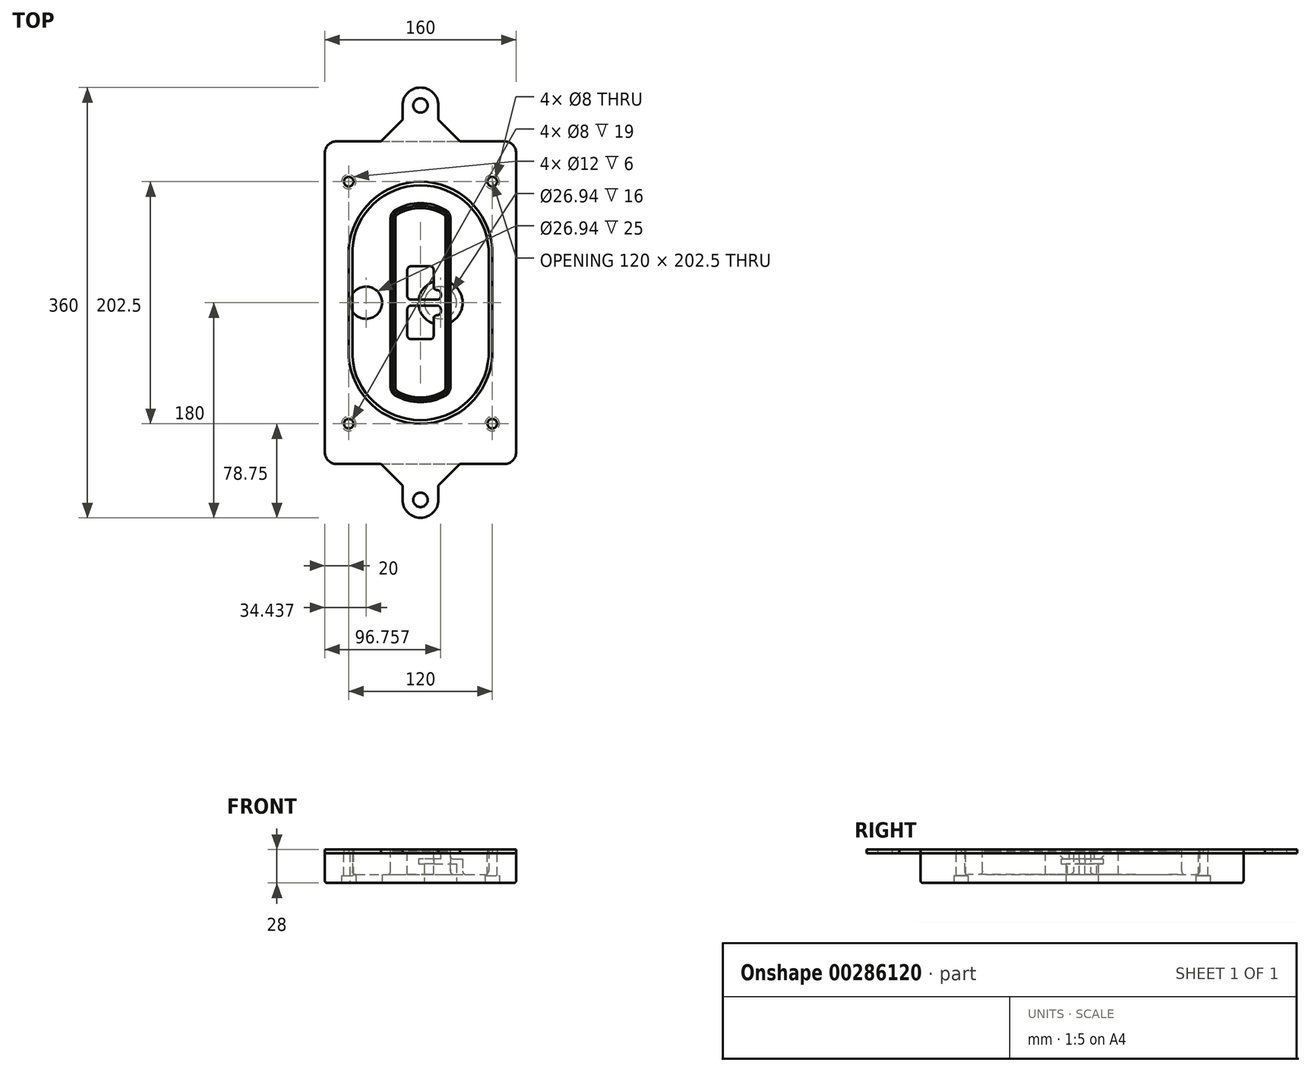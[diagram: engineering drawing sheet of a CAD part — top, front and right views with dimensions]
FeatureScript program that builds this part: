
annotation { "Feature Type Name" : "Feature", "Feature Type Description" : "" }
export const myFeature = defineFeature(function(context is Context, id is Id, definition is map)
    precondition{}
    {
        {
            var Q0;
            Q0=qCreatedBy(makeId("Top.planeOp"),FACE);
            var sketch = newSketch(context, id + "F0", { "sketchPlane" : qUnion([Q0])});
            skPoint(sketch, "E0.rect.middle", {"position": v(0, 0) * mm});
            skLineSegment(sketch, "E1.bottom", {"start": v(-70, -135) * mm, "end": v(70, -135) * mm});
            skLineSegment(sketch, "E1.top", {"start": v(-70, 135) * mm, "end": v(70, 135) * mm});
            skLineSegment(sketch, "E1.left", {"start": v(-80, -125) * mm, "end": v(-80, 125) * mm});
            skLineSegment(sketch, "E1.right", {"start": v(80, -125) * mm, "end": v(80, 125) * mm});
            skLineSegment(sketch, "E2", {"start": v(-80, 135) * mm, "end": v(80, -135) * mm, "construction": true});
            skLineSegment(sketch, "E3", {"start": v(80, 135) * mm, "end": v(-80, -135) * mm, "construction": true});
            skCircle(sketch, "E4", {"center": v(-60, 101.25) * mm, "radius": 4 * mm});
            skCircle(sketch, "E5", {"center": v(60, 101.25) * mm, "radius": 4 * mm});
            skCircle(sketch, "E6", {"center": v(60, -101.25) * mm, "radius": 4 * mm});
            skCircle(sketch, "E7", {"center": v(-60, -101.25) * mm, "radius": 4 * mm});
            skLineSegment(sketch, "E8", {"start": v(-60, 101.25) * mm, "end": v(60, 101.25) * mm, "construction": true});
            skLineSegment(sketch, "E9", {"start": v(60, 101.25) * mm, "end": v(60, -101.25) * mm, "construction": true});
            skLineSegment(sketch, "E10", {"start": v(60, -101.25) * mm, "end": v(-60, -101.25) * mm, "construction": true});
            skLineSegment(sketch, "E11", {"start": v(-60, -101.25) * mm, "end": v(-60, 101.25) * mm, "construction": true});
            skLineSegment(sketch, "E12", {"start": v(-60, 44.66) * mm, "end": v(-60, -44.66) * mm});
            skLineSegment(sketch, "E13", {"start": v(60, 44.66) * mm, "end": v(60, -44.66) * mm});
            skArc(sketch, "E14", {"start": v(59.98, 45.37) * mm, "mid": v(0, 101.25) * mm, "end": v(-59.98, 45.37) * mm});
            skArc(sketch, "E15", {"start": v(-59.98, -45.37) * mm, "mid": v(0, -101.25) * mm, "end": v(59.98, -45.37) * mm});
            skLineSegment(sketch, "E16", {"start": v(-60, 0) * mm, "end": v(60, 0) * mm, "construction": true});
            skPoint(sketch, "E17.visualSharp", {"position": v(-60, -45) * mm});
            skArc(sketch, "E17.filletArc", {"start": v(-60, -44.66) * mm, "mid": v(-60, -45.02) * mm, "end": v(-59.98, -45.37) * mm});
            skPoint(sketch, "E18.visualSharp", {"position": v(-60, 45) * mm});
            skArc(sketch, "E18.filletArc", {"start": v(-59.98, 45.37) * mm, "mid": v(-60, 45.02) * mm, "end": v(-60, 44.66) * mm});
            skPoint(sketch, "E19.visualSharp", {"position": v(60, 45) * mm});
            skArc(sketch, "E19.filletArc", {"start": v(60, 44.66) * mm, "mid": v(60, 45.02) * mm, "end": v(59.98, 45.37) * mm});
            skPoint(sketch, "E20.visualSharp", {"position": v(60, -45) * mm});
            skArc(sketch, "E20.filletArc", {"start": v(59.98, -45.37) * mm, "mid": v(60, -45.02) * mm, "end": v(60, -44.66) * mm});
            skPoint(sketch, "E21.visualSharp", {"position": v(-80, 135) * mm});
            skArc(sketch, "E21.filletArc", {"start": v(-70, 135) * mm, "mid": v(-77.07, 132.07) * mm, "end": v(-80, 125) * mm});
            skPoint(sketch, "E22.visualSharp", {"position": v(80, 135) * mm});
            skArc(sketch, "E22.filletArc", {"start": v(80, 125) * mm, "mid": v(77.07, 132.07) * mm, "end": v(70, 135) * mm});
            skPoint(sketch, "E23.visualSharp", {"position": v(80, -135) * mm});
            skArc(sketch, "E23.filletArc", {"start": v(70, -135) * mm, "mid": v(77.07, -132.07) * mm, "end": v(80, -125) * mm});
            skPoint(sketch, "E24.visualSharp", {"position": v(-80, -135) * mm});
            skArc(sketch, "E24.filletArc", {"start": v(-80, -125) * mm, "mid": v(-77.07, -132.07) * mm, "end": v(-70, -135) * mm});
            skArc(sketch, "E25.0", {"start": v(57, 44.66) * mm, "mid": v(57, 44.9) * mm, "end": v(56.98, 45.16) * mm});
            skLineSegment(sketch, "E25.1", {"start": v(57, 44.66) * mm, "end": v(57, -44.66) * mm});
            skArc(sketch, "E25.2", {"start": v(56.98, -45.16) * mm, "mid": v(57, -44.9) * mm, "end": v(57, -44.66) * mm});
            skArc(sketch, "E25.3", {"start": v(-56.98, -45.16) * mm, "mid": v(0, -98.25) * mm, "end": v(56.98, -45.16) * mm});
            skArc(sketch, "E25.4", {"start": v(-57, -44.66) * mm, "mid": v(-57, -44.9) * mm, "end": v(-56.98, -45.16) * mm});
            skArc(sketch, "E25.5", {"start": v(56.98, 45.16) * mm, "mid": v(0, 98.25) * mm, "end": v(-56.98, 45.16) * mm});
            skLineSegment(sketch, "E25.6", {"start": v(-57, 44.66) * mm, "end": v(-57, -44.66) * mm});
            skArc(sketch, "E25.7", {"start": v(-56.98, 45.16) * mm, "mid": v(-57, 44.9) * mm, "end": v(-57, 44.66) * mm});
            skArc(sketch, "E26.0", {"start": v(-63.97, 45.65) * mm, "mid": v(-64, 45.16) * mm, "end": v(-64, 44.66) * mm});
            skArc(sketch, "E26.1", {"start": v(63.97, 45.65) * mm, "mid": v(0, 105.25) * mm, "end": v(-63.97, 45.65) * mm});
            skArc(sketch, "E26.2", {"start": v(64, 44.66) * mm, "mid": v(64, 45.16) * mm, "end": v(63.97, 45.65) * mm});
            skLineSegment(sketch, "E26.3", {"start": v(64, 44.66) * mm, "end": v(64, -44.66) * mm});
            skArc(sketch, "E26.4", {"start": v(63.97, -45.65) * mm, "mid": v(64, -45.16) * mm, "end": v(64, -44.66) * mm});
            skLineSegment(sketch, "E26.5", {"start": v(-64, 44.66) * mm, "end": v(-64, -44.66) * mm});
            skArc(sketch, "E26.6", {"start": v(-63.97, -45.65) * mm, "mid": v(0, -105.25) * mm, "end": v(63.97, -45.65) * mm});
            skArc(sketch, "E26.7", {"start": v(-64, -44.66) * mm, "mid": v(-64, -45.16) * mm, "end": v(-63.97, -45.65) * mm});
            skSolve(sketch);
        }
        {
            var Q0;
            Q0=makeQuery(id+"F0.imprint","IMPRINT",FACE,{"disambiguationData":[TD([[makeQuery(id+"F0.imprint","IMPRINT",EDGE,{"derivedFrom":sQuery(id+"F0.wireOp",EDGE,"E1.bottom")}),1.0]])]});
            var Q1;
            Q1=makeQuery(id+"F0.imprint","IMPRINT",FACE,{"disambiguationData":[TD([[makeQuery(id+"F0.imprint","IMPRINT",EDGE,{"derivedFrom":sQuery(id+"F0.wireOp",EDGE,"E12")}),1.0]])]});
            var Q2;
            Q2=makeQuery(id+"F0.imprint","IMPRINT",FACE,{"disambiguationData":[TD([[makeQuery(id+"F0.imprint","IMPRINT",EDGE,{"derivedFrom":sQuery(id+"F0.wireOp",EDGE,"E25.0")}),1.0]])]});
            var Q3;
            Q3=makeQuery(id+"F0.imprint","IMPRINT",FACE,{"disambiguationData":[TD([[makeQuery(id+"F0.imprint","IMPRINT",EDGE,{"derivedFrom":sQuery(id+"F0.wireOp",EDGE,"E12")}),-1.0]])]});
            extrude(context, id + "F1", {"entities" : qUnion([Q0, Q1, Q2, Q3]), "oppositeDirection" : true, "depth" : 25 * mm});
        }
        {
            var Q0;
            Q0=makeQuery(id+"F0.imprint","IMPRINT",FACE,{"disambiguationData":[TD([[makeQuery(id+"F0.imprint","IMPRINT",EDGE,{"derivedFrom":sQuery(id+"F0.wireOp",EDGE,"E12")}),1.0]])]});
            extrude(context, id + "F2", {"entities" : qUnion([Q0]), "operationType" : NewBodyOperationType.ADD, "depth" : 3 * mm});
        }
        {
            var Q0;
            Q0=makeQuery(id+"F0.imprint","IMPRINT",FACE,{"disambiguationData":[TD([[makeQuery(id+"F0.imprint","IMPRINT",EDGE,{"derivedFrom":sQuery(id+"F0.wireOp",EDGE,"E25.0")}),1.0]])]});
            extrude(context, id + "F3", {"entities" : qUnion([Q0]), "operationType" : NewBodyOperationType.REMOVE, "oppositeDirection" : true, "depth" : 18 * mm});
        }
        {
            var Q0;
            Q0=makeQuery(id+"F2.opExtrude","CAP_FACE",FACE,{"disambiguationData":[OSD([sQuery(id+"F0.wireOp",EDGE,"E12"),sQuery(id+"F0.wireOp",EDGE,"E13"),sQuery(id+"F0.wireOp",EDGE,"E14"),sQuery(id+"F0.wireOp",EDGE,"E15"),sQuery(id+"F0.wireOp",EDGE,"E17.filletArc"),sQuery(id+"F0.wireOp",EDGE,"E18.filletArc"),sQuery(id+"F0.wireOp",EDGE,"E19.filletArc"),sQuery(id+"F0.wireOp",EDGE,"E20.filletArc"),sQuery(id+"F0.wireOp",EDGE,"E25.0"),sQuery(id+"F0.wireOp",EDGE,"E25.1"),sQuery(id+"F0.wireOp",EDGE,"E25.2"),sQuery(id+"F0.wireOp",EDGE,"E25.3"),sQuery(id+"F0.wireOp",EDGE,"E25.4"),sQuery(id+"F0.wireOp",EDGE,"E25.5"),sQuery(id+"F0.wireOp",EDGE,"E25.6"),sQuery(id+"F0.wireOp",EDGE,"E25.7")])],"isStart":false});
            var sketch = newSketch(context, id + "F4", { "sketchPlane" : qUnion([Q0])});
            skArc(sketch, "E27.0", {"start": v(-20.99, -77.65) * mm, "mid": v(0, -83.25) * mm, "end": v(20.99, -77.65) * mm});
            skArc(sketch, "E28.0", {"start": v(20.99, 77.65) * mm, "mid": v(0, 83.25) * mm, "end": v(-20.99, 77.65) * mm});
            skLineSegment(sketch, "E29", {"start": v(-25, 70.71) * mm, "end": v(-25, -70.71) * mm});
            skLineSegment(sketch, "E30", {"start": v(25, 70.71) * mm, "end": v(25, -70.71) * mm});
            skLineSegment(sketch, "E31", {"start": v(-25, 75.03) * mm, "end": v(25, 75.03) * mm, "construction": true});
            skLineSegment(sketch, "E32", {"start": v(-25, -75.03) * mm, "end": v(25, -75.03) * mm, "construction": true});
            skPoint(sketch, "E33.visualSharp", {"position": v(-25, 75.03) * mm});
            skArc(sketch, "E33.filletArc", {"start": v(-20.99, 77.65) * mm, "mid": v(-23.92, 74.72) * mm, "end": v(-25, 70.71) * mm});
            skPoint(sketch, "E34.visualSharp", {"position": v(25, 75.03) * mm});
            skArc(sketch, "E34.filletArc", {"start": v(25, 70.71) * mm, "mid": v(23.92, 74.72) * mm, "end": v(20.99, 77.65) * mm});
            skPoint(sketch, "E35.visualSharp", {"position": v(25, -75.03) * mm});
            skArc(sketch, "E35.filletArc", {"start": v(20.99, -77.65) * mm, "mid": v(23.92, -74.72) * mm, "end": v(25, -70.71) * mm});
            skPoint(sketch, "E36.visualSharp", {"position": v(-25, -75.03) * mm});
            skArc(sketch, "E36.filletArc", {"start": v(-25, -70.71) * mm, "mid": v(-23.92, -74.72) * mm, "end": v(-20.99, -77.65) * mm});
            skArc(sketch, "E37.0", {"start": v(56.98, 45.16) * mm, "mid": v(0, 98.25) * mm, "end": v(-56.98, 45.16) * mm});
            skArc(sketch, "E37.1", {"start": v(-56.98, 45.16) * mm, "mid": v(-57, 44.9) * mm, "end": v(-57, 44.66) * mm});
            skLineSegment(sketch, "E37.2", {"start": v(-57, 44.66) * mm, "end": v(-57, -44.66) * mm});
            skArc(sketch, "E37.3", {"start": v(-57, -44.66) * mm, "mid": v(-57, -44.9) * mm, "end": v(-56.98, -45.16) * mm});
            skArc(sketch, "E37.4", {"start": v(-56.98, -45.16) * mm, "mid": v(0, -98.25) * mm, "end": v(56.98, -45.16) * mm});
            skArc(sketch, "E37.5", {"start": v(56.98, -45.16) * mm, "mid": v(57, -44.9) * mm, "end": v(57, -44.66) * mm});
            skLineSegment(sketch, "E37.6", {"start": v(57, 44.66) * mm, "end": v(57, -44.66) * mm});
            skArc(sketch, "E37.7", {"start": v(57, 44.66) * mm, "mid": v(57, 44.9) * mm, "end": v(56.98, 45.16) * mm});
            skLineSegment(sketch, "E38.0", {"start": v(23, 70.71) * mm, "end": v(23, -70.71) * mm});
            skArc(sketch, "E38.1", {"start": v(19.99, -75.92) * mm, "mid": v(22.2, -73.72) * mm, "end": v(23, -70.71) * mm});
            skArc(sketch, "E38.2", {"start": v(-19.99, -75.92) * mm, "mid": v(0, -81.25) * mm, "end": v(19.99, -75.92) * mm});
            skArc(sketch, "E38.3", {"start": v(-23, -70.71) * mm, "mid": v(-22.2, -73.72) * mm, "end": v(-19.99, -75.92) * mm});
            skLineSegment(sketch, "E38.4", {"start": v(-23, 70.71) * mm, "end": v(-23, -70.71) * mm});
            skArc(sketch, "E38.5", {"start": v(23, 70.71) * mm, "mid": v(22.2, 73.72) * mm, "end": v(19.99, 75.92) * mm});
            skArc(sketch, "E38.6", {"start": v(-19.99, 75.92) * mm, "mid": v(-22.2, 73.72) * mm, "end": v(-23, 70.71) * mm});
            skArc(sketch, "E38.7", {"start": v(19.99, 75.92) * mm, "mid": v(0, 81.25) * mm, "end": v(-19.99, 75.92) * mm});
            skArc(sketch, "E39.0", {"start": v(21, 70.71) * mm, "mid": v(20.46, 72.72) * mm, "end": v(19, 74.18) * mm});
            skLineSegment(sketch, "E39.1", {"start": v(21, 70.71) * mm, "end": v(21, -70.71) * mm});
            skArc(sketch, "E39.2", {"start": v(19, -74.18) * mm, "mid": v(20.46, -72.72) * mm, "end": v(21, -70.71) * mm});
            skArc(sketch, "E39.3", {"start": v(-19, -74.18) * mm, "mid": v(0, -79.25) * mm, "end": v(19, -74.18) * mm});
            skArc(sketch, "E39.4", {"start": v(-21, -70.71) * mm, "mid": v(-20.46, -72.72) * mm, "end": v(-19, -74.18) * mm});
            skArc(sketch, "E39.5", {"start": v(19, 74.18) * mm, "mid": v(0, 79.25) * mm, "end": v(-19, 74.18) * mm});
            skLineSegment(sketch, "E39.6", {"start": v(-21, 70.71) * mm, "end": v(-21, -70.71) * mm});
            skArc(sketch, "E39.7", {"start": v(-19, 74.18) * mm, "mid": v(-20.46, 72.72) * mm, "end": v(-21, 70.71) * mm});
            skLineSegment(sketch, "E40", {"start": v(-25, 0) * mm, "end": v(25, 0) * mm, "construction": true});
            skLineSegment(sketch, "E41", {"start": v(-11, 5.5) * mm, "end": v(-11, 27.5) * mm});
            skLineSegment(sketch, "E42", {"start": v(-8, 30.5) * mm, "end": v(8, 30.5) * mm});
            skLineSegment(sketch, "E43", {"start": v(11, 27.5) * mm, "end": v(11, 13.5) * mm});
            skLineSegment(sketch, "E44", {"start": v(14, 10.5) * mm, "end": v(14, 10.5) * mm});
            skLineSegment(sketch, "E45", {"start": v(17, 7.5) * mm, "end": v(17, 5.5) * mm});
            skLineSegment(sketch, "E46", {"start": v(14, 2.5) * mm, "end": v(-8, 2.5) * mm});
            skPoint(sketch, "E47.visualSharp", {"position": v(-11, 30.5) * mm});
            skArc(sketch, "E47.filletArc", {"start": v(-8, 30.5) * mm, "mid": v(-10.12, 29.62) * mm, "end": v(-11, 27.5) * mm});
            skPoint(sketch, "E48.visualSharp", {"position": v(11, 30.5) * mm});
            skArc(sketch, "E48.filletArc", {"start": v(11, 27.5) * mm, "mid": v(10.12, 29.62) * mm, "end": v(8, 30.5) * mm});
            skPoint(sketch, "E49.visualSharp", {"position": v(11, 10.5) * mm});
            skArc(sketch, "E49.filletArc", {"start": v(11, 13.5) * mm, "mid": v(11.88, 11.38) * mm, "end": v(14, 10.5) * mm});
            skPoint(sketch, "E50.visualSharp", {"position": v(17, 10.5) * mm});
            skArc(sketch, "E50.filletArc", {"start": v(17, 7.5) * mm, "mid": v(16.12, 9.62) * mm, "end": v(14, 10.5) * mm});
            skPoint(sketch, "E51.visualSharp", {"position": v(17, 2.5) * mm});
            skArc(sketch, "E51.filletArc", {"start": v(14, 2.5) * mm, "mid": v(16.12, 3.38) * mm, "end": v(17, 5.5) * mm});
            skPoint(sketch, "E52.visualSharp", {"position": v(-11, 2.5) * mm});
            skArc(sketch, "E52.filletArc", {"start": v(-11, 5.5) * mm, "mid": v(-10.12, 3.38) * mm, "end": v(-8, 2.5) * mm});
            skLineSegment(sketch, "E53.0.MirrorCS", {"start": v(14, -2.5) * mm, "end": v(-8, -2.5) * mm});
            skArc(sketch, "E54.0.MirrorCS", {"start": v(-11, -5.5) * mm, "mid": v(-10.12, -3.38) * mm, "end": v(-8, -2.5) * mm});
            skLineSegment(sketch, "E55.0.MirrorCS", {"start": v(-11, -5.5) * mm, "end": v(-11, -27.5) * mm});
            skArc(sketch, "E56.0.MirrorCS", {"start": v(-8, -30.5) * mm, "mid": v(-10.12, -29.62) * mm, "end": v(-11, -27.5) * mm});
            skLineSegment(sketch, "E57.0.MirrorCS", {"start": v(-8, -30.5) * mm, "end": v(8, -30.5) * mm});
            skArc(sketch, "E58.0.MirrorCS", {"start": v(11, -27.5) * mm, "mid": v(10.12, -29.62) * mm, "end": v(8, -30.5) * mm});
            skLineSegment(sketch, "E59.0.MirrorCS", {"start": v(11, -27.5) * mm, "end": v(11, -13.5) * mm});
            skArc(sketch, "E60.0.MirrorCS", {"start": v(11, -13.5) * mm, "mid": v(11.88, -11.38) * mm, "end": v(14, -10.5) * mm});
            skArc(sketch, "E61.0.MirrorCS", {"start": v(17, -7.5) * mm, "mid": v(16.12, -9.62) * mm, "end": v(14, -10.5) * mm});
            skLineSegment(sketch, "E62.0.MirrorCS", {"start": v(17, -7.5) * mm, "end": v(17, -5.5) * mm});
            skArc(sketch, "E63.0.MirrorCS", {"start": v(14, -2.5) * mm, "mid": v(16.12, -3.38) * mm, "end": v(17, -5.5) * mm});
            skSolve(sketch);
        }
        {
            var Q0;
            Q0=makeQuery(id+"F4.imprint","IMPRINT",FACE,{"disambiguationData":[TD([[makeQuery(id+"F4.imprint","IMPRINT",EDGE,{"derivedFrom":sQuery(id+"F4.wireOp",EDGE,"E27.0")}),1.0]])]});
            var Q1;
            Q1=makeQuery(id+"F4.imprint","IMPRINT",FACE,{"disambiguationData":[TD([[makeQuery(id+"F4.imprint","IMPRINT",EDGE,{"derivedFrom":sQuery(id+"F4.wireOp",EDGE,"E38.0")}),-1.0]])]});
            var Q2;
            Q2=makeQuery(id+"F4.imprint","IMPRINT",FACE,{"disambiguationData":[TD([[makeQuery(id+"F4.imprint","IMPRINT",EDGE,{"derivedFrom":sQuery(id+"F4.wireOp",EDGE,"E39.0")}),1.0]])]});
            extrude(context, id + "F5", {"entities" : qUnion([Q0, Q1, Q2]), "operationType" : NewBodyOperationType.ADD, "endBound" : BoundingType.UP_TO_NEXT, "oppositeDirection" : true, "depth" : 25 * mm});
        }
        {
            var Q0;
            Q0=makeQuery(id+"F4.imprint","IMPRINT",FACE,{"disambiguationData":[TD([[makeQuery(id+"F4.imprint","IMPRINT",EDGE,{"derivedFrom":sQuery(id+"F4.wireOp",EDGE,"E38.0")}),-1.0]])]});
            extrude(context, id + "F6", {"entities" : qUnion([Q0]), "operationType" : NewBodyOperationType.REMOVE, "oppositeDirection" : true, "depth" : 2 * mm});
        }
        {
            var Q0;
            Q0=makeQuery(id+"F1.opExtrude","CAP_FACE",FACE,{"disambiguationData":[OSD([sQuery(id+"F0.wireOp",EDGE,"E1.bottom"),sQuery(id+"F0.wireOp",EDGE,"E1.top"),sQuery(id+"F0.wireOp",EDGE,"E1.left"),sQuery(id+"F0.wireOp",EDGE,"E1.right"),sQuery(id+"F0.wireOp",EDGE,"E4"),sQuery(id+"F0.wireOp",EDGE,"E5"),sQuery(id+"F0.wireOp",EDGE,"E6"),sQuery(id+"F0.wireOp",EDGE,"E7"),sQuery(id+"F0.wireOp",EDGE,"E21.filletArc"),sQuery(id+"F0.wireOp",EDGE,"E22.filletArc"),sQuery(id+"F0.wireOp",EDGE,"E23.filletArc"),sQuery(id+"F0.wireOp",EDGE,"E24.filletArc")])],"isStart":false});
            var sketch = newSketch(context, id + "F7", { "sketchPlane" : qUnion([Q0])});
            skCircle(sketch, "E64", {"center": v(16.76, 0) * mm, "radius": 13.47 * mm});
            skCircle(sketch, "E65", {"center": v(-45.56, 0) * mm, "radius": 13.47 * mm});
            skLineSegment(sketch, "E66", {"start": v(80, 0) * mm, "end": v(-80, 0) * mm});
            skCircle(sketch, "E67", {"center": v(16.76, 0) * mm, "radius": 18.47 * mm});
            skCircle(sketch, "E68", {"center": v(60, -101.25) * mm, "radius": 6 * mm});
            skCircle(sketch, "E69", {"center": v(-60, -101.25) * mm, "radius": 6 * mm});
            skCircle(sketch, "E70", {"center": v(-60, 101.25) * mm, "radius": 6 * mm});
            skCircle(sketch, "E71", {"center": v(60, 101.25) * mm, "radius": 6 * mm});
            skSolve(sketch);
        }
        {
            var Q0;
            {var subQ1=sQuery(id+"F7.wireOp",EDGE,"E66");var subQ4=sQuery(id+"F7.wireOp",EDGE,"E64");var subQ6=makeQuery(id+"F7.imprint","INTERSECT",VERTEX,{"disambiguationData":[OD(0.0)],"derivedFrom":[subQ4,subQ1]});Q0=makeQuery(id+"F7.imprint","IMPRINT",FACE,{"disambiguationData":[TD([[makeQuery(id+"F7.imprint","IMPRINT",EDGE,{"disambiguationData":[TD([[subQ6,-1.0]])],"derivedFrom":subQ4}),-1.0]])]});}
            var Q1;
            {var subQ0=sQuery(id+"F7.wireOp",EDGE,"E66");var subQ1=sQuery(id+"F7.wireOp",EDGE,"E64");var subQ3=makeQuery(id+"F7.imprint","INTERSECT",VERTEX,{"disambiguationData":[OD(0.0)],"derivedFrom":[subQ1,subQ0]});Q1=makeQuery(id+"F7.imprint","IMPRINT",FACE,{"disambiguationData":[TD([[makeQuery(id+"F7.imprint","IMPRINT",EDGE,{"disambiguationData":[TD([[subQ3,-1.0]])],"derivedFrom":subQ1}),1.0]])]});}
            var Q2;
            {var subQ0=sQuery(id+"F7.wireOp",EDGE,"E66");var subQ1=sQuery(id+"F7.wireOp",EDGE,"E64");var subQ3=makeQuery(id+"F7.imprint","INTERSECT",VERTEX,{"disambiguationData":[OD(0.0)],"derivedFrom":[subQ1,subQ0]});Q2=makeQuery(id+"F7.imprint","IMPRINT",FACE,{"disambiguationData":[TD([[makeQuery(id+"F7.imprint","IMPRINT",EDGE,{"disambiguationData":[TD([[subQ3,1.0]])],"derivedFrom":subQ1}),1.0]])]});}
            var Q3;
            {var subQ1=sQuery(id+"F7.wireOp",EDGE,"E66");var subQ4=sQuery(id+"F7.wireOp",EDGE,"E64");var subQ6=makeQuery(id+"F7.imprint","INTERSECT",VERTEX,{"disambiguationData":[OD(0.0)],"derivedFrom":[subQ4,subQ1]});Q3=makeQuery(id+"F7.imprint","IMPRINT",FACE,{"disambiguationData":[TD([[makeQuery(id+"F7.imprint","IMPRINT",EDGE,{"disambiguationData":[TD([[subQ6,1.0]])],"derivedFrom":subQ4}),-1.0]])]});}
            extrude(context, id + "F8", {"entities" : qUnion([Q0, Q1, Q2, Q3]), "operationType" : NewBodyOperationType.ADD, "oppositeDirection" : true, "depth" : 20 * mm});
        }
        {
            var Q0;
            {var subQ0=sQuery(id+"F7.wireOp",EDGE,"E66");var subQ1=sQuery(id+"F7.wireOp",EDGE,"E64");var subQ3=makeQuery(id+"F7.imprint","INTERSECT",VERTEX,{"disambiguationData":[OD(0.0)],"derivedFrom":[subQ1,subQ0]});Q0=makeQuery(id+"F7.imprint","IMPRINT",FACE,{"disambiguationData":[TD([[makeQuery(id+"F7.imprint","IMPRINT",EDGE,{"disambiguationData":[TD([[subQ3,-1.0]])],"derivedFrom":subQ1}),1.0]])]});}
            var Q1;
            {var subQ0=sQuery(id+"F7.wireOp",EDGE,"E66");var subQ1=sQuery(id+"F7.wireOp",EDGE,"E64");var subQ3=makeQuery(id+"F7.imprint","INTERSECT",VERTEX,{"disambiguationData":[OD(0.0)],"derivedFrom":[subQ1,subQ0]});Q1=makeQuery(id+"F7.imprint","IMPRINT",FACE,{"disambiguationData":[TD([[makeQuery(id+"F7.imprint","IMPRINT",EDGE,{"disambiguationData":[TD([[subQ3,1.0]])],"derivedFrom":subQ1}),1.0]])]});}
            extrude(context, id + "F9", {"entities" : qUnion([Q0, Q1]), "operationType" : NewBodyOperationType.REMOVE, "oppositeDirection" : true, "depth" : 16 * mm});
        }
        {
            var Q0;
            {var subQ0=sQuery(id+"F7.wireOp",EDGE,"E66");var subQ1=sQuery(id+"F7.wireOp",EDGE,"E65");var subQ3=makeQuery(id+"F7.imprint","INTERSECT",VERTEX,{"disambiguationData":[OD(0.0)],"derivedFrom":[subQ1,subQ0]});Q0=makeQuery(id+"F7.imprint","IMPRINT",FACE,{"disambiguationData":[TD([[makeQuery(id+"F7.imprint","IMPRINT",EDGE,{"disambiguationData":[TD([[subQ3,-1.0]])],"derivedFrom":subQ1}),1.0]])]});}
            var Q1;
            {var subQ0=sQuery(id+"F7.wireOp",EDGE,"E66");var subQ1=sQuery(id+"F7.wireOp",EDGE,"E65");var subQ3=makeQuery(id+"F7.imprint","INTERSECT",VERTEX,{"disambiguationData":[OD(0.0)],"derivedFrom":[subQ1,subQ0]});Q1=makeQuery(id+"F7.imprint","IMPRINT",FACE,{"disambiguationData":[TD([[makeQuery(id+"F7.imprint","IMPRINT",EDGE,{"disambiguationData":[TD([[subQ3,1.0]])],"derivedFrom":subQ1}),1.0]])]});}
            extrude(context, id + "F10", {"entities" : qUnion([Q0, Q1]), "operationType" : NewBodyOperationType.REMOVE, "oppositeDirection" : true, "depth" : 25 * mm});
        }
        {
            var Q0;
            Q0=makeQuery(id+"F7.imprint","IMPRINT",FACE,{"disambiguationData":[TD([[makeQuery(id+"F7.imprint","IMPRINT",EDGE,{"derivedFrom":sQuery(id+"F7.wireOp",EDGE,"E68")}),1.0]])]});
            var Q1;
            Q1=makeQuery(id+"F7.imprint","IMPRINT",FACE,{"disambiguationData":[TD([[makeQuery(id+"F7.imprint","IMPRINT",EDGE,{"derivedFrom":makeQuery(id+"F1.opExtrude","CAP_EDGE",EDGE,{"disambiguationData":[OSD([sQuery(id+"F0.wireOp",EDGE,"E5")])],"isStart":false})}),-1.0]])]});
            var Q2;
            Q2=makeQuery(id+"F7.imprint","IMPRINT",FACE,{"disambiguationData":[TD([[makeQuery(id+"F7.imprint","IMPRINT",EDGE,{"derivedFrom":sQuery(id+"F7.wireOp",EDGE,"E69")}),1.0]])]});
            var Q3;
            Q3=makeQuery(id+"F7.imprint","IMPRINT",FACE,{"disambiguationData":[TD([[makeQuery(id+"F7.imprint","IMPRINT",EDGE,{"derivedFrom":makeQuery(id+"F1.opExtrude","CAP_EDGE",EDGE,{"disambiguationData":[OSD([sQuery(id+"F0.wireOp",EDGE,"E4")])],"isStart":false})}),-1.0]])]});
            var Q4;
            Q4=makeQuery(id+"F7.imprint","IMPRINT",FACE,{"disambiguationData":[TD([[makeQuery(id+"F7.imprint","IMPRINT",EDGE,{"derivedFrom":sQuery(id+"F7.wireOp",EDGE,"E70")}),1.0]])]});
            var Q5;
            Q5=makeQuery(id+"F7.imprint","IMPRINT",FACE,{"disambiguationData":[TD([[makeQuery(id+"F7.imprint","IMPRINT",EDGE,{"derivedFrom":makeQuery(id+"F1.opExtrude","CAP_EDGE",EDGE,{"disambiguationData":[OSD([sQuery(id+"F0.wireOp",EDGE,"E7")])],"isStart":false})}),-1.0]])]});
            var Q6;
            Q6=makeQuery(id+"F7.imprint","IMPRINT",FACE,{"disambiguationData":[TD([[makeQuery(id+"F7.imprint","IMPRINT",EDGE,{"derivedFrom":sQuery(id+"F7.wireOp",EDGE,"E71")}),1.0]])]});
            var Q7;
            Q7=makeQuery(id+"F7.imprint","IMPRINT",FACE,{"disambiguationData":[TD([[makeQuery(id+"F7.imprint","IMPRINT",EDGE,{"derivedFrom":makeQuery(id+"F1.opExtrude","CAP_EDGE",EDGE,{"disambiguationData":[OSD([sQuery(id+"F0.wireOp",EDGE,"E6")])],"isStart":false})}),-1.0]])]});
            extrude(context, id + "F11", {"entities" : qUnion([Q0, Q1, Q2, Q3, Q4, Q5, Q6, Q7]), "operationType" : NewBodyOperationType.REMOVE, "oppositeDirection" : true, "depth" : 6 * mm});
        }
        {
            var Q0;
            Q0=makeQuery(id+"F9.boolean.opBoolean","COPY",FACE,{"derivedFrom":makeQuery(id+"F9.opExtrude","CAP_FACE",FACE,{"disambiguationData":[OSD([sQuery(id+"F7.wireOp",EDGE,"E64")])],"isStart":false})});
            var sketch = newSketch(context, id + "F12", { "sketchPlane" : qUnion([Q0])});
            skArc(sketch, "E72.0", {"start": v(11, 17.55) * mm, "mid": v(2.57, 11.82) * mm, "end": v(-1.54, 2.5) * mm});
            skArc(sketch, "E72.1", {"start": v(-1.54, -2.5) * mm, "mid": v(2.57, -11.82) * mm, "end": v(11, -17.55) * mm});
            skLineSegment(sketch, "E73", {"start": v(-1.54, -2.5) * mm, "end": v(14, -2.5) * mm});
            skLineSegment(sketch, "E74.0", {"start": v(14, 2.5) * mm, "end": v(-1.54, 2.5) * mm});
            skArc(sketch, "E74.1", {"start": v(14, 2.5) * mm, "mid": v(16.12, 3.38) * mm, "end": v(17, 5.5) * mm});
            skLineSegment(sketch, "E74.2", {"start": v(17, 7.5) * mm, "end": v(17, 5.5) * mm});
            skArc(sketch, "E74.3", {"start": v(17, 7.5) * mm, "mid": v(16.12, 9.62) * mm, "end": v(14, 10.5) * mm});
            skArc(sketch, "E74.4", {"start": v(11, 13.5) * mm, "mid": v(11.88, 11.38) * mm, "end": v(14, 10.5) * mm});
            skLineSegment(sketch, "E74.5", {"start": v(11, 17.55) * mm, "end": v(11, 13.5) * mm});
            skLineSegment(sketch, "E74.7", {"start": v(14, -2.5) * mm, "end": v(-1.54, -2.5) * mm});
            skArc(sketch, "E74.8", {"start": v(14, -2.5) * mm, "mid": v(16.12, -3.38) * mm, "end": v(17, -5.5) * mm});
            skLineSegment(sketch, "E74.9", {"start": v(17, -7.5) * mm, "end": v(17, -5.5) * mm});
            skArc(sketch, "E74.10", {"start": v(17, -7.5) * mm, "mid": v(16.12, -9.62) * mm, "end": v(14, -10.5) * mm});
            skArc(sketch, "E74.11", {"start": v(11, -13.5) * mm, "mid": v(11.88, -11.38) * mm, "end": v(14, -10.5) * mm});
            skLineSegment(sketch, "E74.12", {"start": v(11, -17.55) * mm, "end": v(11, -13.5) * mm});
            skPoint(sketch, "E75.orphan", {"position": v(11, -27.5) * mm});
            skPoint(sketch, "E76.orphan", {"position": v(-8, -2.5) * mm});
            skPoint(sketch, "E77.orphan", {"position": v(-8, 2.5) * mm});
            skPoint(sketch, "E78.orphan", {"position": v(11, 27.5) * mm});
            skSolve(sketch);
        }
        {
            var Q0;
            {var subQ7=sQuery(id+"F12.wireOp",EDGE,"E72.0");var subQ14=sQuery(id+"F12.wireOp",EDGE,"E72.1");var subQ16=sQuery(id+"F12.wireOp",EDGE,"E74.1");var subQ18=sQuery(id+"F12.wireOp",EDGE,"E74.8");Q0=qUnion([makeQuery(id+"F12.imprint","IMPRINT",FACE,{"disambiguationData":[TD([[makeQuery(id+"F12.imprint","IMPRINT",EDGE,{"derivedFrom":subQ7}),1.0]])]}),makeQuery(id+"F12.imprint","IMPRINT",FACE,{"disambiguationData":[TD([[makeQuery(id+"F12.imprint","IMPRINT",EDGE,{"derivedFrom":subQ14}),1.0]])]}),makeQuery(id+"F12.imprint","IMPRINT",FACE,{"disambiguationData":[TD([[makeQuery(id+"F12.imprint","IMPRINT",EDGE,{"derivedFrom":subQ16}),1.0]])]}),makeQuery(id+"F12.imprint","IMPRINT",FACE,{"disambiguationData":[TD([[makeQuery(id+"F12.imprint","IMPRINT",EDGE,{"derivedFrom":subQ18}),-1.0]])]})]);}
            var Q1;
            Q1=makeQuery(id+"F5.boolean.opBoolean","SPLIT",FACE,{"disambiguationData":[TD([makeQuery(id+"F5.opExtrude","SWEPT_FACE",FACE,{"disambiguationData":[OSD([sQuery(id+"F4.wireOp",EDGE,"E41")])]})])],"derivedFrom":makeQuery(id+"F3.boolean.opBoolean","COPY",FACE,{"derivedFrom":makeQuery(id+"F3.opExtrude","CAP_FACE",FACE,{"disambiguationData":[OSD([sQuery(id+"F0.wireOp",EDGE,"E25.0"),sQuery(id+"F0.wireOp",EDGE,"E25.1"),sQuery(id+"F0.wireOp",EDGE,"E25.2"),sQuery(id+"F0.wireOp",EDGE,"E25.3"),sQuery(id+"F0.wireOp",EDGE,"E25.4"),sQuery(id+"F0.wireOp",EDGE,"E25.5"),sQuery(id+"F0.wireOp",EDGE,"E25.6"),sQuery(id+"F0.wireOp",EDGE,"E25.7")])],"isStart":false})})});
            extrude(context, id + "F13", {"entities" : qUnion([Q0]), "operationType" : NewBodyOperationType.REMOVE, "endBound" : BoundingType.UP_TO_SURFACE, "endBoundEntityFace" : qUnion([Q1]), "depth" : 25 * mm});
        }
        {
            var Q0;
            Q0=makeQuery(id+"F3.boolean.opBoolean","COPY",EDGE,{"derivedFrom":makeQuery(id+"F3.opExtrude","CAP_EDGE",EDGE,{"disambiguationData":[OSD([sQuery(id+"F0.wireOp",EDGE,"E25.6")])],"isStart":false})});
            var Q1;
            Q1=makeQuery(id+"F8.boolean.opBoolean","INTERSECT",EDGE,{"derivedFrom":[makeQuery(id+"F5.opExtrude","SWEPT_FACE",FACE,{"disambiguationData":[OSD([sQuery(id+"F4.wireOp",EDGE,"E30")])]}),makeQuery(id+"F8.opExtrude","CAP_FACE",FACE,{"disambiguationData":[OSD([sQuery(id+"F7.wireOp",EDGE,"E67")])],"isStart":false})]});
            var Q2;
            Q2=makeQuery(id+"F8.boolean.opBoolean","INTERSECT",EDGE,{"disambiguationData":[OD(1.0)],"derivedFrom":[makeQuery(id+"F5.opExtrude","SWEPT_FACE",FACE,{"disambiguationData":[OSD([sQuery(id+"F4.wireOp",EDGE,"E30")])]}),makeQuery(id+"F8.opExtrude","SWEPT_FACE",FACE,{"disambiguationData":[OSD([sQuery(id+"F7.wireOp",EDGE,"E67")])]})]});
            var Q3;
            {var subQ0=sQuery(id+"F4.wireOp",EDGE,"E30");Q3=makeQuery(id+"F8.boolean.opBoolean","SPLIT",EDGE,{"disambiguationData":[TD([makeQuery(id+"F5.opExtrude","SWEPT_FACE",FACE,{"disambiguationData":[OSD([sQuery(id+"F4.wireOp",EDGE,"E35.filletArc")])]})])],"derivedFrom":makeQuery(id+"F5.opExtrude","CAP_EDGE",EDGE,{"disambiguationData":[OSD([subQ0])],"isStart":false})});}
            var Q4;
            {var subQ0=sQuery(id+"F0.wireOp",EDGE,"E25.7");var subQ1=sQuery(id+"F0.wireOp",EDGE,"E25.1");var subQ2=sQuery(id+"F0.wireOp",EDGE,"E25.6");var subQ3=sQuery(id+"F0.wireOp",EDGE,"E25.5");var subQ4=sQuery(id+"F0.wireOp",EDGE,"E25.4");var subQ5=sQuery(id+"F0.wireOp",EDGE,"E25.0");var subQ6=sQuery(id+"F0.wireOp",EDGE,"E25.2");var subQ7=sQuery(id+"F0.wireOp",EDGE,"E25.3");Q4=makeQuery(id+"F8.boolean.opBoolean","INTERSECT",EDGE,{"derivedFrom":[makeQuery(id+"F5.boolean.opBoolean","SPLIT",FACE,{"disambiguationData":[TD([makeQuery(id+"F2.opExtrude","SWEPT_FACE",FACE,{"disambiguationData":[OSD([subQ5])]})])],"derivedFrom":makeQuery(id+"F3.boolean.opBoolean","COPY",FACE,{"derivedFrom":makeQuery(id+"F3.opExtrude","CAP_FACE",FACE,{"disambiguationData":[OSD([subQ5,subQ1,subQ6,subQ7,subQ4,subQ3,subQ2,subQ0])],"isStart":false})})}),makeQuery(id+"F8.opExtrude","SWEPT_FACE",FACE,{"disambiguationData":[OSD([sQuery(id+"F7.wireOp",EDGE,"E67")])]})]});}
            var Q5;
            Q5=makeQuery(id+"F8.boolean.opBoolean","INTERSECT",EDGE,{"disambiguationData":[OD(0.0)],"derivedFrom":[makeQuery(id+"F5.opExtrude","SWEPT_FACE",FACE,{"disambiguationData":[OSD([sQuery(id+"F4.wireOp",EDGE,"E30")])]}),makeQuery(id+"F8.opExtrude","SWEPT_FACE",FACE,{"disambiguationData":[OSD([sQuery(id+"F7.wireOp",EDGE,"E67")])]})]});
            fillet(context, id + "F14", {"entities" : qUnion([Q0, Q1, Q2, Q3, Q4, Q5]), "radius" : 3 * mm, "tangentPropagation" : true, "allowEdgeOverflow" : false});
        }
        {
            var Q0;
            Q0=makeQuery(id+"F1.opExtrude","CAP_EDGE",EDGE,{"disambiguationData":[OSD([sQuery(id+"F0.wireOp",EDGE,"E1.bottom")])],"isStart":false});
            fillet(context, id + "F15", {"entities" : qUnion([Q0]), "radius" : 2 * mm, "tangentPropagation" : true, "allowEdgeOverflow" : false});
        }
        {
            var Q0;
            {var subQ0=sQuery(id+"F0.wireOp",EDGE,"E21.filletArc");var subQ1=sQuery(id+"F0.wireOp",EDGE,"E7");var subQ2=sQuery(id+"F0.wireOp",EDGE,"E6");var subQ3=sQuery(id+"F0.wireOp",EDGE,"E5");var subQ4=sQuery(id+"F0.wireOp",EDGE,"E4");var subQ5=sQuery(id+"F0.wireOp",EDGE,"E22.filletArc");var subQ6=sQuery(id+"F0.wireOp",EDGE,"E1.bottom");var subQ7=sQuery(id+"F0.wireOp",EDGE,"E1.right");var subQ8=sQuery(id+"F0.wireOp",EDGE,"E1.top");var subQ9=sQuery(id+"F0.wireOp",EDGE,"E1.left");var subQ10=sQuery(id+"F0.wireOp",EDGE,"E23.filletArc");var subQ11=sQuery(id+"F0.wireOp",EDGE,"E24.filletArc");Q0=makeQuery(id+"F2.boolean.opBoolean","SPLIT",FACE,{"disambiguationData":[TD([makeQuery(id+"F1.opExtrude","SWEPT_FACE",FACE,{"disambiguationData":[OSD([subQ6])]})])],"derivedFrom":makeQuery(id+"F1.opExtrude","CAP_FACE",FACE,{"disambiguationData":[OSD([subQ6,subQ8,subQ9,subQ7,subQ4,subQ3,subQ2,subQ1,subQ0,subQ5,subQ10,subQ11])],"isStart":true})});}
            var sketch = newSketch(context, id + "F16", { "sketchPlane" : qUnion([Q0])});
            skCircle(sketch, "E79", {"center": v(0, 165) * mm, "radius": 6 * mm});
            skLineSegment(sketch, "E80", {"start": v(0, 165) * mm, "end": v(0, 135) * mm, "construction": true});
            skLineSegment(sketch, "E81", {"start": v(-33, 135) * mm, "end": v(-15, 153) * mm});
            skLineSegment(sketch, "E82", {"start": v(-15, 153) * mm, "end": v(-15, 165) * mm});
            skLineSegment(sketch, "E83", {"start": v(33, 135) * mm, "end": v(15, 153) * mm});
            skLineSegment(sketch, "E84", {"start": v(15, 153) * mm, "end": v(15, 165) * mm});
            skArc(sketch, "E85", {"start": v(15, 165) * mm, "mid": v(0, 180) * mm, "end": v(-15, 165) * mm});
            skArc(sketch, "E86.0", {"start": v(80, 125) * mm, "mid": v(77.07, 132.07) * mm, "end": v(70, 135) * mm});
            skLineSegment(sketch, "E86.1", {"start": v(-70, 135) * mm, "end": v(70, 135) * mm});
            skCircle(sketch, "E86.2", {"center": v(60, 101.25) * mm, "radius": 4 * mm});
            skLineSegment(sketch, "E86.3", {"start": v(80, -125) * mm, "end": v(80, 125) * mm});
            skArc(sketch, "E86.4", {"start": v(59.98, 45.37) * mm, "mid": v(0, 101.25) * mm, "end": v(-59.98, 45.37) * mm});
            skArc(sketch, "E86.5", {"start": v(60, 44.66) * mm, "mid": v(60, 45.02) * mm, "end": v(59.98, 45.37) * mm});
            skLineSegment(sketch, "E86.6", {"start": v(60, 44.66) * mm, "end": v(60, -44.66) * mm});
            skArc(sketch, "E86.7", {"start": v(59.98, -45.37) * mm, "mid": v(60, -45.02) * mm, "end": v(60, -44.66) * mm});
            skArc(sketch, "E86.8", {"start": v(-59.98, -45.37) * mm, "mid": v(0, -101.25) * mm, "end": v(59.98, -45.37) * mm});
            skArc(sketch, "E86.9", {"start": v(-60, -44.66) * mm, "mid": v(-60, -45.02) * mm, "end": v(-59.98, -45.37) * mm});
            skLineSegment(sketch, "E86.10", {"start": v(-60, 44.66) * mm, "end": v(-60, -44.66) * mm});
            skArc(sketch, "E86.11", {"start": v(-59.98, 45.37) * mm, "mid": v(-60, 45.02) * mm, "end": v(-60, 44.66) * mm});
            skLineSegment(sketch, "E86.12", {"start": v(-80, -125) * mm, "end": v(-80, 125) * mm});
            skArc(sketch, "E86.13", {"start": v(-70, 135) * mm, "mid": v(-77.07, 132.07) * mm, "end": v(-80, 125) * mm});
            skCircle(sketch, "E86.14", {"center": v(-60, 101.25) * mm, "radius": 4 * mm});
            skCircle(sketch, "E86.15", {"center": v(-60, -101.25) * mm, "radius": 4 * mm});
            skArc(sketch, "E86.16", {"start": v(-80, -125) * mm, "mid": v(-77.07, -132.07) * mm, "end": v(-70, -135) * mm});
            skLineSegment(sketch, "E86.17", {"start": v(-70, -135) * mm, "end": v(70, -135) * mm});
            skCircle(sketch, "E86.18", {"center": v(60, -101.25) * mm, "radius": 4 * mm});
            skArc(sketch, "E86.19", {"start": v(70, -135) * mm, "mid": v(77.07, -132.07) * mm, "end": v(80, -125) * mm});
            skLineSegment(sketch, "E87", {"start": v(-80, 0) * mm, "end": v(80, 0) * mm, "construction": true});
            skLineSegment(sketch, "E88.MirrorCS", {"start": v(-33, -135) * mm, "end": v(-15, -153) * mm});
            skLineSegment(sketch, "E89.MirrorCS", {"start": v(-15, -153) * mm, "end": v(-15, -165) * mm});
            skArc(sketch, "E90.MirrorCS", {"start": v(15, -165) * mm, "mid": v(0, -180) * mm, "end": v(-15, -165) * mm});
            skCircle(sketch, "E91.MirrorC", {"center": v(0, -165) * mm, "radius": 6 * mm});
            skLineSegment(sketch, "E92.MirrorCS", {"start": v(15, -153) * mm, "end": v(15, -165) * mm});
            skLineSegment(sketch, "E93.MirrorCS", {"start": v(33, -135) * mm, "end": v(15, -153) * mm});
            skLineSegment(sketch, "E94.MirrorCS", {"start": v(0, -165) * mm, "end": v(0, -135) * mm, "construction": true});
            skSolve(sketch);
        }
        {
            var Q0;
            Q0 = qSketchRegion(id + "F16", true);
            var Q1;
            Q1=makeQuery(id+"F2.opExtrude","CAP_FACE",FACE,{"disambiguationData":[OSD([sQuery(id+"F0.wireOp",EDGE,"E12"),sQuery(id+"F0.wireOp",EDGE,"E13"),sQuery(id+"F0.wireOp",EDGE,"E14"),sQuery(id+"F0.wireOp",EDGE,"E15"),sQuery(id+"F0.wireOp",EDGE,"E17.filletArc"),sQuery(id+"F0.wireOp",EDGE,"E18.filletArc"),sQuery(id+"F0.wireOp",EDGE,"E19.filletArc"),sQuery(id+"F0.wireOp",EDGE,"E20.filletArc"),sQuery(id+"F0.wireOp",EDGE,"E25.0"),sQuery(id+"F0.wireOp",EDGE,"E25.1"),sQuery(id+"F0.wireOp",EDGE,"E25.2"),sQuery(id+"F0.wireOp",EDGE,"E25.3"),sQuery(id+"F0.wireOp",EDGE,"E25.4"),sQuery(id+"F0.wireOp",EDGE,"E25.5"),sQuery(id+"F0.wireOp",EDGE,"E25.6"),sQuery(id+"F0.wireOp",EDGE,"E25.7")])],"isStart":false});
            extrude(context, id + "F17", {"entities" : qUnion([Q0]), "endBound" : BoundingType.UP_TO_SURFACE, "endBoundEntityFace" : qUnion([Q1]), "depth" : 25 * mm});
        }
    });
